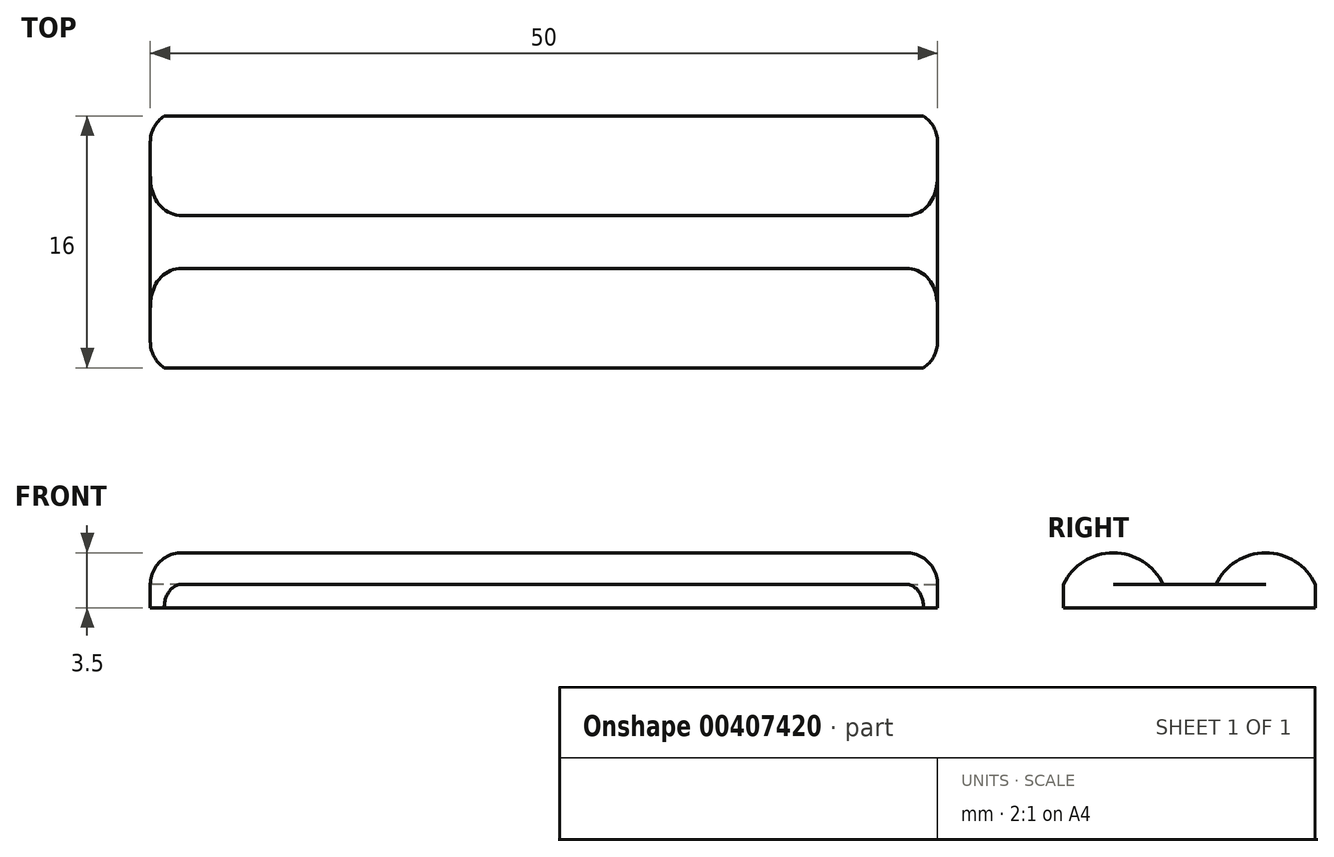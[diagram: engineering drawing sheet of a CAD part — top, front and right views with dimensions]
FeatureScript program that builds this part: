
annotation { "Feature Type Name" : "Feature", "Feature Type Description" : "" }
export const myFeature = defineFeature(function(context is Context, id is Id, definition is map)
    precondition{}
    {
        {
            var Q0;
            Q0=qCreatedBy(makeId("Top.planeOp"),FACE);
            var sketch = newSketch(context, id + "F0", { "sketchPlane" : qUnion([Q0])});
            skLineSegment(sketch, "E0.bottom", {"start": v(25, 8) * mm, "end": v(-25, 8) * mm});
            skLineSegment(sketch, "E0.top", {"start": v(25, -8) * mm, "end": v(-25, -8) * mm});
            skLineSegment(sketch, "E0.left", {"start": v(25, 8) * mm, "end": v(25, -8) * mm});
            skLineSegment(sketch, "E0.right", {"start": v(-25, 8) * mm, "end": v(-25, -8) * mm});
            skPoint(sketch, "E0.middle", {"position": v(0, 0) * mm});
            skSolve(sketch);
        }
        {
            var Q0;
            Q0 = qSketchRegion(id + "F0", true);
            extrude(context, id + "F1", {"entities" : qUnion([Q0]), "oppositeDirection" : true, "depth" : 1.5 * mm});
        }
        {
            var Q0;
            Q0=makeQuery(id+"F1.opExtrude","SWEPT_FACE",FACE,{"disambiguationData":[OSD([sQuery(id+"F0.wireOp",EDGE,"E0.right")])]});
            var sketch = newSketch(context, id + "F2", { "sketchPlane" : qUnion([Q0])});
            skCircle(sketch, "E1", {"center": v(-4.84, -1.5) * mm, "radius": 3.5 * mm});
            skCircle(sketch, "E2", {"center": v(4.84, -1.5) * mm, "radius": 3.5 * mm});
            skLineSegment(sketch, "E3.bottom", {"start": v(-10, 0) * mm, "end": v(10, 0) * mm});
            skLineSegment(sketch, "E3.top", {"start": v(-10, -8) * mm, "end": v(10, -8) * mm});
            skLineSegment(sketch, "E3.left", {"start": v(-10, 0) * mm, "end": v(-10, -8) * mm});
            skLineSegment(sketch, "E3.right", {"start": v(10, 0) * mm, "end": v(10, -8) * mm});
            skPoint(sketch, "E3.middle", {"position": v(0, -4) * mm});
            skSolve(sketch);
        }
        {
            var Q0;
            {var subQ0=sQuery(id+"F2.wireOp",EDGE,"E3.bottom");var subQ1=sQuery(id+"F2.wireOp",EDGE,"E1");var subQ3=makeQuery(id+"F2.imprint","INTERSECT",VERTEX,{"derivedFrom":[subQ1,subQ0]});Q0=makeQuery(id+"F2.imprint","IMPRINT",FACE,{"disambiguationData":[TD([[makeQuery(id+"F2.imprint","IMPRINT",EDGE,{"disambiguationData":[TD([[subQ3,-1.0]])],"derivedFrom":subQ1}),1.0]])]});}
            var Q1;
            {var subQ0=sQuery(id+"F2.wireOp",EDGE,"E3.bottom");var subQ1=sQuery(id+"F2.wireOp",EDGE,"E2");var subQ3=makeQuery(id+"F2.imprint","INTERSECT",VERTEX,{"derivedFrom":[subQ1,subQ0]});Q1=makeQuery(id+"F2.imprint","IMPRINT",FACE,{"disambiguationData":[TD([[makeQuery(id+"F2.imprint","IMPRINT",EDGE,{"disambiguationData":[TD([[subQ3,1.0]])],"derivedFrom":subQ1}),1.0]])]});}
            extrude(context, id + "F3", {"entities" : qUnion([Q0, Q1]), "operationType" : NewBodyOperationType.ADD, "oppositeDirection" : true, "depth" : 50 * mm});
        }
        {
            var Q0;
            Q0=makeQuery(id+"F3.opExtrude","CAP_EDGE",EDGE,{"disambiguationData":[OSD([sQuery(id+"F2.wireOp",EDGE,"E2")])],"isStart":true});
            var Q1;
            Q1=makeQuery(id+"F3.opExtrude","CAP_EDGE",EDGE,{"disambiguationData":[OSD([sQuery(id+"F2.wireOp",EDGE,"E1")])],"isStart":true});
            var Q2;
            Q2=makeQuery(id+"F3.opExtrude","CAP_EDGE",EDGE,{"disambiguationData":[OSD([sQuery(id+"F2.wireOp",EDGE,"E2")])],"isStart":false});
            var Q3;
            Q3=makeQuery(id+"F3.opExtrude","CAP_EDGE",EDGE,{"disambiguationData":[OSD([sQuery(id+"F2.wireOp",EDGE,"E1")])],"isStart":false});
            fillet(context, id + "F4", {"entities" : qUnion([Q0, Q1, Q2, Q3]), "radius" : 2 * mm, "tangentPropagation" : true, "allowEdgeOverflow" : false});
        }
    });
